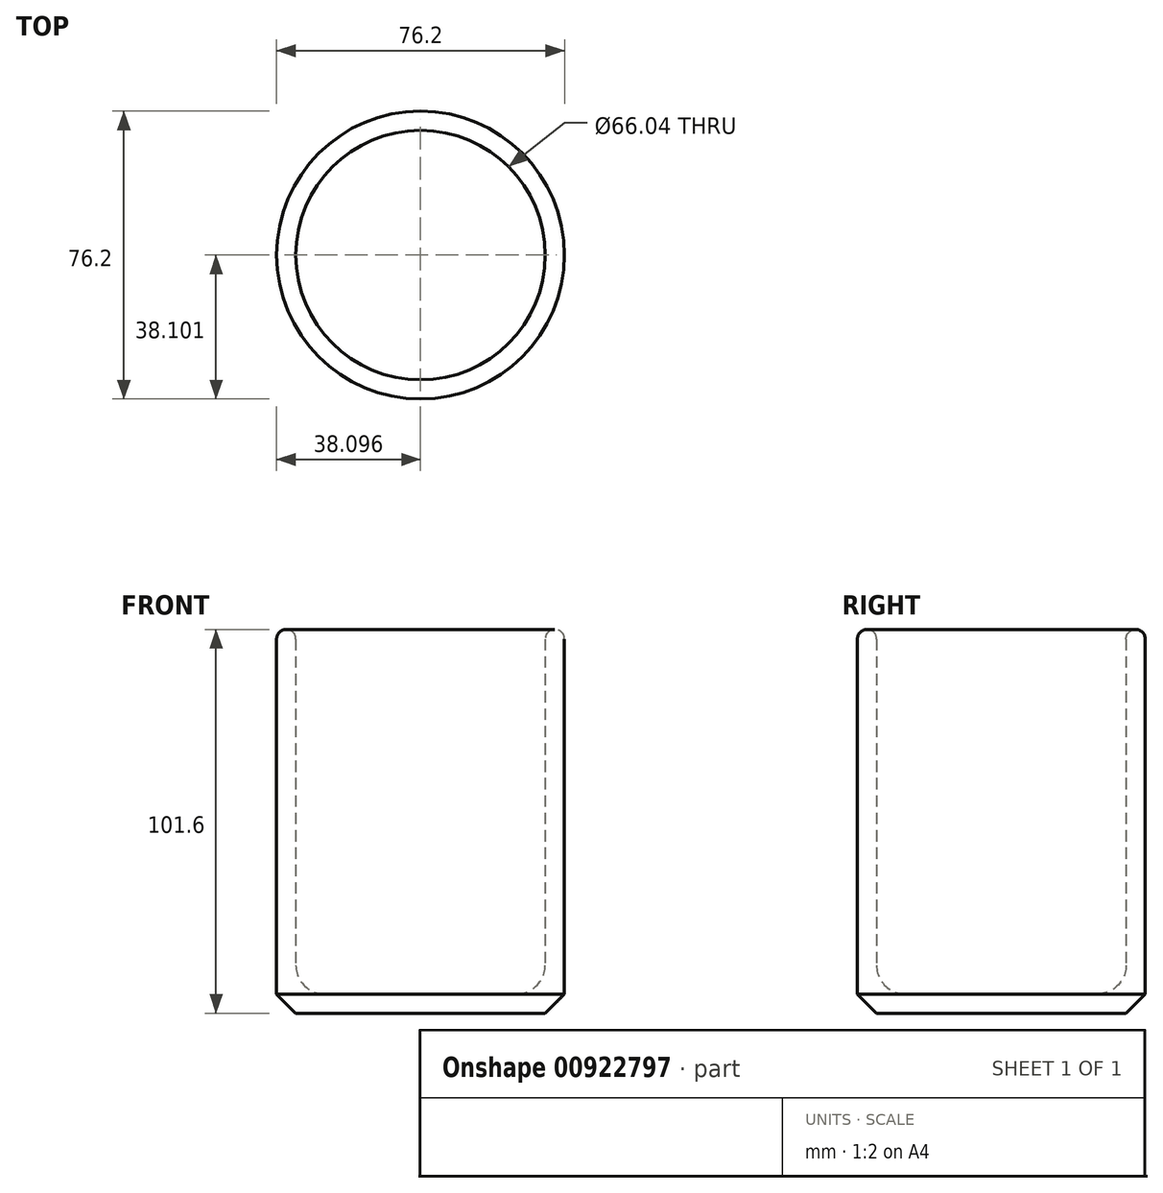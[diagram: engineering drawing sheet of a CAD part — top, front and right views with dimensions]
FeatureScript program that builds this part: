
annotation { "Feature Type Name" : "Feature", "Feature Type Description" : "" }
export const myFeature = defineFeature(function(context is Context, id is Id, definition is map)
    precondition{}
    {
        {
            var Q0;
            Q0=qCreatedBy(makeId("Top.planeOp"),FACE);
            var sketch = newSketch(context, id + "F0", { "sketchPlane" : qUnion([Q0])});
            skCircle(sketch, "E0", {"center": v(-51.53, 6.25) * mm, "radius": 38.1 * mm});
            skSolve(sketch);
        }
        {
            var Q0;
            Q0=makeQuery(id+"F0.imprint","IMPRINT",FACE,{"disambiguationData":[TD([[makeQuery(id+"F0.imprint","IMPRINT",EDGE,{"derivedFrom":sQuery(id+"F0.wireOp",EDGE,"E0")}),1.0]])]});
            extrude(context, id + "F1", {"entities" : qUnion([Q0]), "depth" : 101.6 * mm, "offsetDistance" : 25.4 * mm});
        }
        {
            var Q0;
            Q0=makeQuery(id+"F1.opExtrude","CAP_FACE",FACE,{"disambiguationData":[OSD([sQuery(id+"F0.wireOp",EDGE,"E0")])],"isStart":false});
            shell(context, id + "F2", {"entities" : qUnion([Q0]), "thickness" : 5.08 * mm});
        }
        {
            var Q0;
            {var subQ0=sQuery(id+"F0.wireOp",EDGE,"E0");Q0=makeQuery(id+"F2.opShell","OFFSET_EDGE",EDGE,{"disambiguationData":[OSD([subQ0]),TDD([makeQuery(id+"F1.opExtrude","CAP_EDGE",EDGE,{"disambiguationData":[OSD([subQ0])],"isStart":true})])]});}
            fillet(context, id + "F3", {"entities" : qUnion([Q0]), "radius" : 7.62 * mm, "tangentPropagation" : true, "allowEdgeOverflow" : false});
        }
        {
            var Q0;
            {var subQ0=sQuery(id+"F0.wireOp",EDGE,"E0");Q0=makeQuery(id+"F2.opShell","OFFSET_EDGE",EDGE,{"disambiguationData":[OSD([subQ0]),TDD([makeQuery(id+"F1.opExtrude","CAP_EDGE",EDGE,{"disambiguationData":[OSD([subQ0])],"isStart":false})])]});}
            var Q1;
            Q1=makeQuery(id+"F1.opExtrude","CAP_EDGE",EDGE,{"disambiguationData":[OSD([sQuery(id+"F0.wireOp",EDGE,"E0")])],"isStart":false});
            fillet(context, id + "F4", {"entities" : qUnion([Q0, Q1]), "radius" : 2.54 * mm, "tangentPropagation" : true, "allowEdgeOverflow" : false});
        }
        {
            var Q0;
            Q0=makeQuery(id+"F1.opExtrude","CAP_EDGE",EDGE,{"disambiguationData":[OSD([sQuery(id+"F0.wireOp",EDGE,"E0")])],"isStart":true});
            chamfer(context, id + "F5", {"entities" : qUnion([Q0]), "width" : 5.08 * mm, "tangentPropagation" : true});
        }
    });
